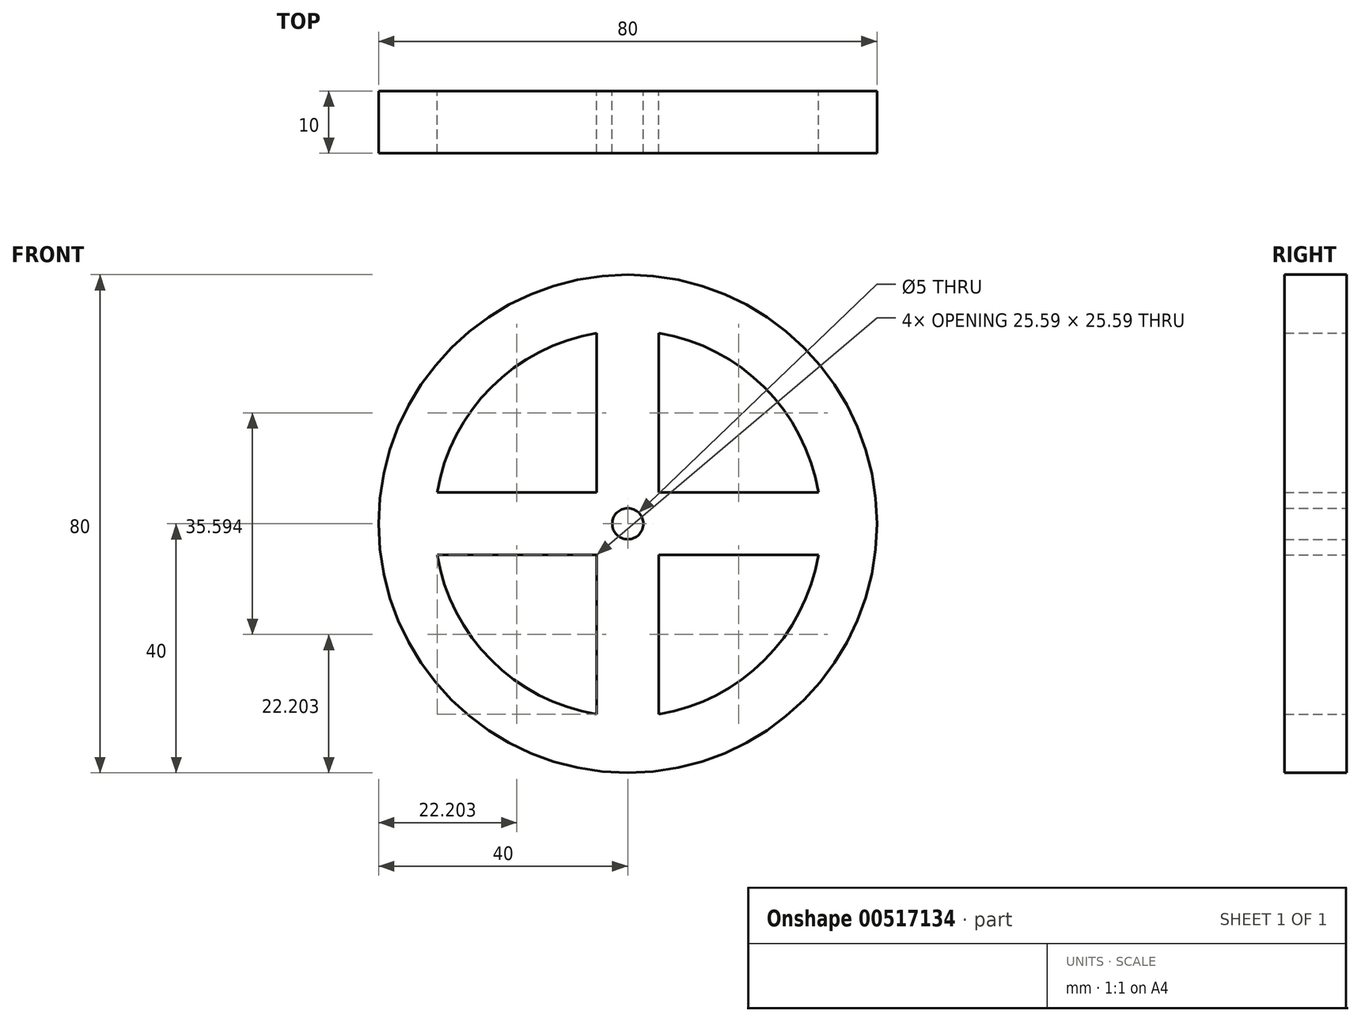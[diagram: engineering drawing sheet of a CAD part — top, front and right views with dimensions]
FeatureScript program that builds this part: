
annotation { "Feature Type Name" : "Feature", "Feature Type Description" : "" }
export const myFeature = defineFeature(function(context is Context, id is Id, definition is map)
    precondition{}
    {
        {
            var Q0;
            Q0=qCreatedBy(makeId("Front.planeOp"),FACE);
            var sketch = newSketch(context, id + "F0", { "sketchPlane" : qUnion([Q0])});
            skCircle(sketch, "E0", {"center": v(0, 0) * mm, "radius": 40 * mm});
            skArc(sketch, "E1", {"start": v(-5, 30.6) * mm, "mid": v(-21.92, 21.92) * mm, "end": v(-30.6, 5) * mm});
            skCircle(sketch, "E2", {"center": v(0, 0) * mm, "radius": 2.5 * mm});
            skLineSegment(sketch, "E3", {"start": v(-2.5, 0) * mm, "end": v(0, 0) * mm});
            skLineSegment(sketch, "E4", {"start": v(0, 0) * mm, "end": v(2.5, 0) * mm});
            skLineSegment(sketch, "E5", {"start": v(0, -2.5) * mm, "end": v(0, 0) * mm});
            skLineSegment(sketch, "E6", {"start": v(0, 0) * mm, "end": v(0, 2.5) * mm});
            skLineSegment(sketch, "E7.0", {"start": v(5, 5) * mm, "end": v(5, 30.6) * mm});
            skLineSegment(sketch, "E8.0", {"start": v(-5, 5) * mm, "end": v(-5, 30.6) * mm});
            skLineSegment(sketch, "E9.0", {"start": v(5, -5) * mm, "end": v(30.6, -5) * mm});
            skLineSegment(sketch, "E10.0", {"start": v(5, 5) * mm, "end": v(30.6, 5) * mm});
            skLineSegment(sketch, "E11.0", {"start": v(-5, -40) * mm, "end": v(-5, -39.69) * mm});
            skLineSegment(sketch, "E12.0", {"start": v(5, -40) * mm, "end": v(5, -39.69) * mm});
            skLineSegment(sketch, "E13.0", {"start": v(-40, 5) * mm, "end": v(-39.69, 5) * mm});
            skLineSegment(sketch, "E14.0", {"start": v(-40, -5) * mm, "end": v(-39.69, -5) * mm});
            skLineSegment(sketch, "E15.trimOffspring", {"start": v(39.69, 5) * mm, "end": v(40, 5) * mm});
            skLineSegment(sketch, "E16.trimOffspring", {"start": v(39.69, -5) * mm, "end": v(40, -5) * mm});
            skLineSegment(sketch, "E17.trimOffspring", {"start": v(5, -30.6) * mm, "end": v(5, -5) * mm});
            skLineSegment(sketch, "E18.trimOffspring", {"start": v(5, 39.69) * mm, "end": v(5, 40) * mm});
            skLineSegment(sketch, "E19.trimOffspring", {"start": v(-5, 39.69) * mm, "end": v(-5, 40) * mm});
            skLineSegment(sketch, "E20.trimOffspring", {"start": v(-30.6, 5) * mm, "end": v(-5, 5) * mm});
            skPoint(sketch, "E21.orphan", {"position": v(-40, 0) * mm});
            skLineSegment(sketch, "E22.trimOffspring", {"start": v(-30.6, -5) * mm, "end": v(-5, -5) * mm});
            skLineSegment(sketch, "E23.trimOffspring", {"start": v(-5, -30.6) * mm, "end": v(-5, -5) * mm});
            skPoint(sketch, "E24.orphan", {"position": v(0, -40) * mm});
            skArc(sketch, "E25.trimOffspring", {"start": v(30.6, 5) * mm, "mid": v(21.92, 21.92) * mm, "end": v(5, 30.6) * mm});
            skArc(sketch, "E26.trimOffspring", {"start": v(-30.6, -5) * mm, "mid": v(-21.92, -21.92) * mm, "end": v(-5, -30.6) * mm});
            skArc(sketch, "E27.trimOffspring", {"start": v(5, -30.6) * mm, "mid": v(21.92, -21.92) * mm, "end": v(30.6, -5) * mm});
            skSolve(sketch);
        }
        {
            var Q0;
            Q0=makeQuery(id+"F0.imprint","IMPRINT",FACE,{"disambiguationData":[TD([[makeQuery(id+"F0.imprint","IMPRINT",EDGE,{"derivedFrom":sQuery(id+"F0.wireOp",EDGE,"E1")}),-1.0]])]});
            extrude(context, id + "F1", {"entities" : qUnion([Q0]), "depth" : 10 * mm, "offsetDistance" : 25 * mm});
        }
    });
